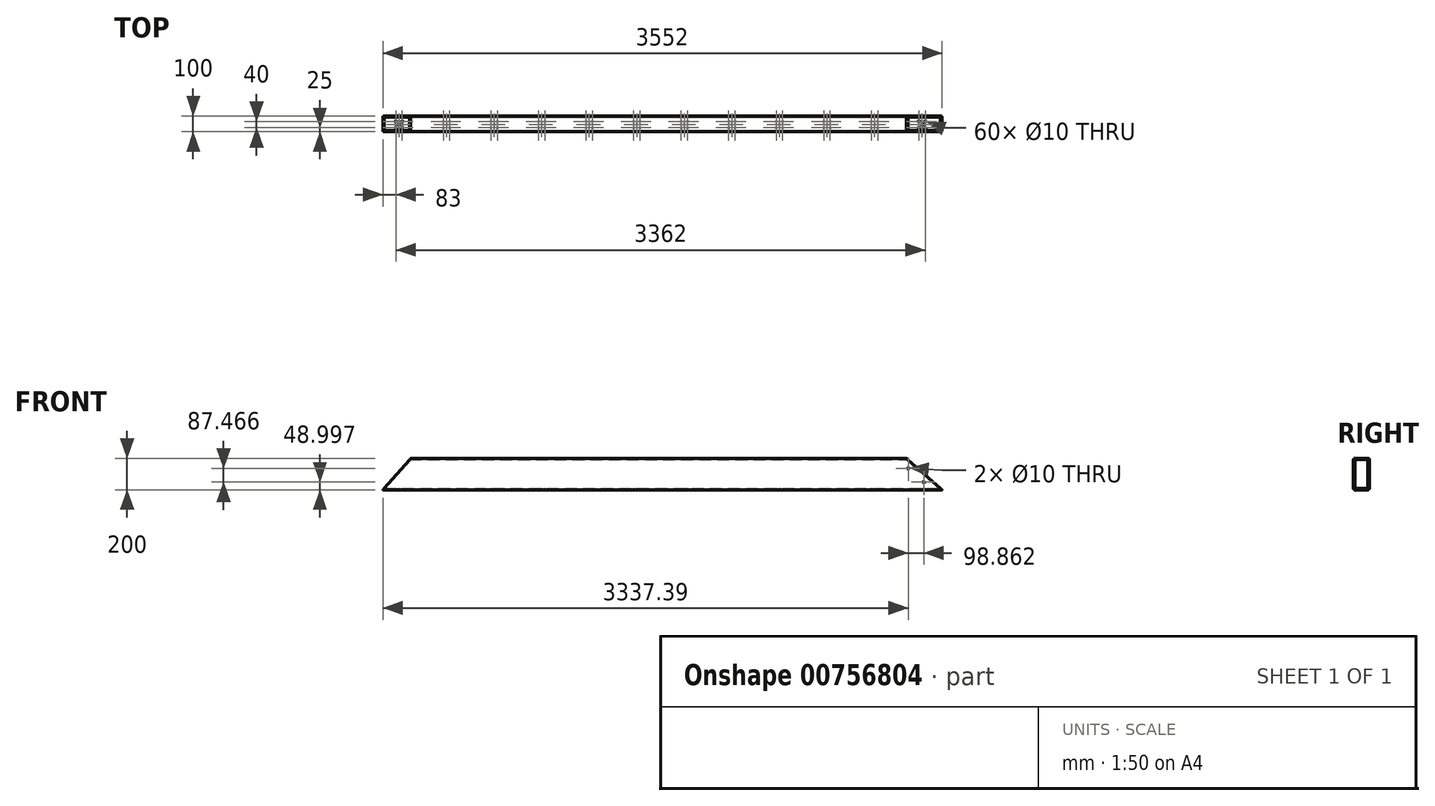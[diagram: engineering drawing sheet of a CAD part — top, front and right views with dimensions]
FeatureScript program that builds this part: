
annotation { "Feature Type Name" : "Feature", "Feature Type Description" : "" }
export const myFeature = defineFeature(function(context is Context, id is Id, definition is map)
    precondition{}
    {
        {
            var Q0;
            Q0=qCreatedBy(makeId("Front.planeOp"),FACE);
            var sketch = newSketch(context, id + "F0", { "sketchPlane" : qUnion([Q0])});
            skLineSegment(sketch, "E0.bottom", {"start": v(280.88, 430.04) * mm, "end": v(-3263.12, 430.04) * mm});
            skLineSegment(sketch, "E0.top", {"start": v(280.88, 230.04) * mm, "end": v(-3263.12, 230.04) * mm});
            skLineSegment(sketch, "E0.left", {"start": v(280.88, 430.04) * mm, "end": v(280.88, 230.04) * mm});
            skLineSegment(sketch, "E0.right", {"start": v(-3263.12, 430.04) * mm, "end": v(-3263.12, 230.04) * mm});
            skSolve(sketch);
        }
        {
            var Q0;
            Q0 = qSketchRegion(id + "F0", true);
            extrude(context, id + "F1", {"entities" : qUnion([Q0]), "depth" : 100 * mm, "offsetDistance" : 25 * mm});
        }
        {
            var Q0;
            Q0=makeQuery(id+"F1.opExtrude","SWEPT_FACE",FACE,{"disambiguationData":[OSD([sQuery(id+"F0.wireOp",EDGE,"E0.left")])]});
            var sketch = newSketch(context, id + "F2", { "sketchPlane" : qUnion([Q0])});
            skLineSegment(sketch, "E1.bottom", {"start": v(-92, 422.04) * mm, "end": v(-8, 422.04) * mm});
            skLineSegment(sketch, "E1.top", {"start": v(-92, 238.04) * mm, "end": v(-8, 238.04) * mm});
            skLineSegment(sketch, "E1.left", {"start": v(-92, 422.04) * mm, "end": v(-92, 238.04) * mm});
            skLineSegment(sketch, "E1.right", {"start": v(-8, 422.04) * mm, "end": v(-8, 238.04) * mm});
            skSolve(sketch);
        }
        {
            var Q0;
            Q0=makeQuery(id+"F2.imprint","IMPRINT",FACE,{"disambiguationData":[TD([[makeQuery(id+"F2.imprint","IMPRINT",EDGE,{"derivedFrom":sQuery(id+"F2.wireOp",EDGE,"E1.bottom")}),-1.0]])]});
            extrude(context, id + "F3", {"entities" : qUnion([Q0]), "operationType" : NewBodyOperationType.REMOVE, "oppositeDirection" : true, "depth" : 3550 * mm, "offsetDistance" : 25 * mm});
        }
        {
            var Q0;
            Q0=makeQuery(id+"F1.opExtrude","SWEPT_FACE",FACE,{"disambiguationData":[OSD([sQuery(id+"F0.wireOp",EDGE,"E0.bottom")])]});
            var sketch = newSketch(context, id + "F4", { "sketchPlane" : qUnion([Q0])});
            skCircle(sketch, "E2", {"center": v(-1234.85, -45) * mm, "radius": 5 * mm});
            skCircle(sketch, "E3", {"center": v(-1254.85, -75) * mm, "radius": 5 * mm});
            skCircle(sketch, "E4", {"center": v(-1214.85, -75) * mm, "radius": 5 * mm});
            skCircle(sketch, "E5", {"center": v(-1254.85, -25) * mm, "radius": 5 * mm});
            skCircle(sketch, "E6", {"center": v(-1214.85, -25) * mm, "radius": 5 * mm});
            skSolve(sketch);
        }
        {
            var Q0;
            Q0=makeQuery(id+"F1.opExtrude","SWEPT_FACE",FACE,{"disambiguationData":[OSD([sQuery(id+"F0.wireOp",EDGE,"E0.left")])]});
            var Q1;
            Q1=sQuery(id+"F4.wireOp",EDGE,"E3");
            var Q2;
            Q2=sQuery(id+"F4.wireOp",EDGE,"E5");
            var Q3;
            Q3=sQuery(id+"F4.wireOp",EDGE,"E6");
            var Q4;
            Q4=sQuery(id+"F4.wireOp",EDGE,"E4");
            var Q5;
            Q5=sQuery(id+"F4.wireOp",EDGE,"E2");
            extrude(context, id + "F5", {"entities" : qUnion([Q0]), "operationType" : NewBodyOperationType.ADD, "surfaceEntities" : qUnion([Q1, Q2, Q3, Q4, Q5]), "depth" : 8 * mm, "offsetDistance" : 25 * mm});
        }
        {
            var Q0;
            Q0=makeQuery(id+"F1.opExtrude","SWEPT_FACE",FACE,{"disambiguationData":[OSD([sQuery(id+"F0.wireOp",EDGE,"E0.top")])]});
            var sketch = newSketch(context, id + "F6", { "sketchPlane" : qUnion([Q0])});
            skCircle(sketch, "E7", {"center": v(-3180.12, 75) * mm, "radius": 5 * mm});
            skCircle(sketch, "E8", {"center": v(-3140.12, 75) * mm, "radius": 5 * mm});
            skCircle(sketch, "E9", {"center": v(-3160.12, 55) * mm, "radius": 5 * mm});
            skCircle(sketch, "E10", {"center": v(-3180.12, 35) * mm, "radius": 5 * mm});
            skCircle(sketch, "E11", {"center": v(-3140.12, 35) * mm, "radius": 5 * mm});
            skCircle(sketch, "E12", {"center": v(-2878.12, 75) * mm, "radius": 5 * mm});
            skCircle(sketch, "E13", {"center": v(-2838.12, 75) * mm, "radius": 5 * mm});
            skCircle(sketch, "E14", {"center": v(-2858.12, 55) * mm, "radius": 5 * mm});
            skCircle(sketch, "E15", {"center": v(-2878.12, 35) * mm, "radius": 5 * mm});
            skCircle(sketch, "E16", {"center": v(-2838.12, 35) * mm, "radius": 5 * mm});
            skCircle(sketch, "E17", {"center": v(-2576.12, 75) * mm, "radius": 5 * mm});
            skCircle(sketch, "E18", {"center": v(-2536.12, 75) * mm, "radius": 5 * mm});
            skCircle(sketch, "E19", {"center": v(-2556.12, 55) * mm, "radius": 5 * mm});
            skCircle(sketch, "E20", {"center": v(-2576.12, 35) * mm, "radius": 5 * mm});
            skCircle(sketch, "E21", {"center": v(-2536.12, 35) * mm, "radius": 5 * mm});
            skCircle(sketch, "E22", {"center": v(-2274.12, 75) * mm, "radius": 5 * mm});
            skCircle(sketch, "E23", {"center": v(-2234.12, 75) * mm, "radius": 5 * mm});
            skCircle(sketch, "E24", {"center": v(-2254.12, 55) * mm, "radius": 5 * mm});
            skCircle(sketch, "E25", {"center": v(-2274.12, 35) * mm, "radius": 5 * mm});
            skCircle(sketch, "E26", {"center": v(-2234.12, 35) * mm, "radius": 5 * mm});
            skCircle(sketch, "E27", {"center": v(-1972.12, 75) * mm, "radius": 5 * mm});
            skCircle(sketch, "E28", {"center": v(-1932.12, 75) * mm, "radius": 5 * mm});
            skCircle(sketch, "E29", {"center": v(-1952.12, 55) * mm, "radius": 5 * mm});
            skCircle(sketch, "E30", {"center": v(-1972.12, 35) * mm, "radius": 5 * mm});
            skCircle(sketch, "E31", {"center": v(-1932.12, 35) * mm, "radius": 5 * mm});
            skCircle(sketch, "E32", {"center": v(-1670.12, 75) * mm, "radius": 5 * mm});
            skCircle(sketch, "E33", {"center": v(-1630.12, 75) * mm, "radius": 5 * mm});
            skCircle(sketch, "E34", {"center": v(-1650.12, 55) * mm, "radius": 5 * mm});
            skCircle(sketch, "E35", {"center": v(-1670.12, 35) * mm, "radius": 5 * mm});
            skCircle(sketch, "E36", {"center": v(-1630.12, 35) * mm, "radius": 5 * mm});
            skCircle(sketch, "E37", {"center": v(-1368.12, 75) * mm, "radius": 5 * mm});
            skCircle(sketch, "E38", {"center": v(-1328.12, 75) * mm, "radius": 5 * mm});
            skCircle(sketch, "E39", {"center": v(-1348.12, 55) * mm, "radius": 5 * mm});
            skCircle(sketch, "E40", {"center": v(-1368.12, 35) * mm, "radius": 5 * mm});
            skCircle(sketch, "E41", {"center": v(-1328.12, 35) * mm, "radius": 5 * mm});
            skCircle(sketch, "E42", {"center": v(-1066.12, 75) * mm, "radius": 5 * mm});
            skCircle(sketch, "E43", {"center": v(-1026.12, 75) * mm, "radius": 5 * mm});
            skCircle(sketch, "E44", {"center": v(-1046.12, 55) * mm, "radius": 5 * mm});
            skCircle(sketch, "E45", {"center": v(-1066.12, 35) * mm, "radius": 5 * mm});
            skCircle(sketch, "E46", {"center": v(-1026.12, 35) * mm, "radius": 5 * mm});
            skCircle(sketch, "E47", {"center": v(-764.12, 75) * mm, "radius": 5 * mm});
            skCircle(sketch, "E48", {"center": v(-724.12, 75) * mm, "radius": 5 * mm});
            skCircle(sketch, "E49", {"center": v(-744.12, 55) * mm, "radius": 5 * mm});
            skCircle(sketch, "E50", {"center": v(-764.12, 35) * mm, "radius": 5 * mm});
            skCircle(sketch, "E51", {"center": v(-724.12, 35) * mm, "radius": 5 * mm});
            skCircle(sketch, "E52", {"center": v(-160.12, 75) * mm, "radius": 5 * mm});
            skCircle(sketch, "E53", {"center": v(-120.12, 75) * mm, "radius": 5 * mm});
            skCircle(sketch, "E54", {"center": v(-140.12, 55) * mm, "radius": 5 * mm});
            skCircle(sketch, "E55", {"center": v(-160.12, 35) * mm, "radius": 5 * mm});
            skCircle(sketch, "E56", {"center": v(-120.12, 35) * mm, "radius": 5 * mm});
            skCircle(sketch, "E57", {"center": v(141.88, 75) * mm, "radius": 5 * mm});
            skCircle(sketch, "E58", {"center": v(181.88, 75) * mm, "radius": 5 * mm});
            skCircle(sketch, "E59", {"center": v(161.88, 55) * mm, "radius": 5 * mm});
            skCircle(sketch, "E60", {"center": v(141.88, 35) * mm, "radius": 5 * mm});
            skCircle(sketch, "E61", {"center": v(181.88, 35) * mm, "radius": 5 * mm});
            skCircle(sketch, "E62", {"center": v(-462.12, 75) * mm, "radius": 5 * mm});
            skCircle(sketch, "E63", {"center": v(-422.12, 75) * mm, "radius": 5 * mm});
            skCircle(sketch, "E64", {"center": v(-442.12, 55) * mm, "radius": 5 * mm});
            skCircle(sketch, "E65", {"center": v(-462.12, 35) * mm, "radius": 5 * mm});
            skCircle(sketch, "E66", {"center": v(-422.12, 35) * mm, "radius": 5 * mm});
            skSolve(sketch);
        }
        {
            var Q0;
            Q0 = qSketchRegion(id + "F6", true);
            extrude(context, id + "F7", {"entities" : qUnion([Q0]), "operationType" : NewBodyOperationType.REMOVE, "oppositeDirection" : true, "depth" : 8 * mm, "offsetDistance" : 25 * mm});
        }
        {
            var Q0;
            {var subQ0=sQuery(id+"F0.wireOp",EDGE,"E0.left");Q0=makeQuery(id+"F5.boolean.opBoolean","MERGE",FACE,{"derivedFrom":[makeQuery(id+"F1.opExtrude","CAP_FACE",FACE,{"disambiguationData":[OSD([sQuery(id+"F0.wireOp",EDGE,"E0.bottom"),sQuery(id+"F0.wireOp",EDGE,"E0.top"),subQ0,sQuery(id+"F0.wireOp",EDGE,"E0.right")])],"isStart":true}),makeQuery(id+"F5.opExtrude","SWEPT_FACE",FACE,{"disambiguationData":[OSD([subQ0]),TDD([makeQuery(id+"F1.opExtrude","CAP_EDGE",EDGE,{"disambiguationData":[OSD([subQ0])],"isStart":true})])]})]});}
            var sketch = newSketch(context, id + "F8", { "sketchPlane" : qUnion([Q0])});
            skLineSegment(sketch, "E67", {"start": v(3086.18, 430.04) * mm, "end": v(3263.12, 230.04) * mm});
            skLineSegment(sketch, "E68", {"start": v(-62.82, 430.04) * mm, "end": v(-288.88, 230.04) * mm});
            skSolve(sketch);
        }
        {
            var Q0;
            {var subQ0=sQuery(id+"F8.wireOp",EDGE,"E68");Q0=makeQuery(id+"F8.imprint","IMPRINT",FACE,{"disambiguationData":[TD([[makeQuery(id+"F8.imprint","IMPRINT",EDGE,{"derivedFrom":subQ0}),-1.0]])]});}
            var Q1;
            Q1=sQuery(id+"F8.wireOp",EDGE,"E68");
            extrude(context, id + "F9", {"entities" : qUnion([Q0]), "operationType" : NewBodyOperationType.REMOVE, "surfaceEntities" : qUnion([Q1]), "oppositeDirection" : true, "depth" : 100 * mm, "offsetDistance" : 25 * mm});
        }
        {
            var Q0;
            {var subQ0=sQuery(id+"F8.wireOp",EDGE,"E67");Q0=makeQuery(id+"F8.imprint","IMPRINT",FACE,{"disambiguationData":[TD([[makeQuery(id+"F8.imprint","IMPRINT",EDGE,{"derivedFrom":subQ0}),1.0]])]});}
            var Q1;
            Q1=sQuery(id+"F8.wireOp",EDGE,"E67");
            extrude(context, id + "F10", {"entities" : qUnion([Q0]), "operationType" : NewBodyOperationType.REMOVE, "surfaceEntities" : qUnion([Q1]), "oppositeDirection" : true, "depth" : 100 * mm, "offsetDistance" : 25 * mm});
        }
        {
            var Q0;
            {var subQ0=sQuery(id+"F0.wireOp",EDGE,"E0.left");var subQ1=sQuery(id+"F0.wireOp",EDGE,"E0.top");Q0=makeQuery(id+"F5.boolean.opBoolean","MERGE",EDGE,{"derivedFrom":[makeQuery(id+"F1.opExtrude","CAP_EDGE",EDGE,{"disambiguationData":[OSD([subQ1])],"isStart":true}),makeQuery(id+"F5.opExtrude","SWEPT_EDGE",EDGE,{"disambiguationData":[OSD([subQ1,subQ0]),TDD([makeQuery(id+"F1.opExtrude","CAP_VERTEX",VERTEX,{"disambiguationData":[OSD([subQ1,subQ0])],"isStart":true})])]})]});}
            var Q1;
            {var subQ0=sQuery(id+"F0.wireOp",EDGE,"E0.left");var subQ1=sQuery(id+"F0.wireOp",EDGE,"E0.top");Q1=makeQuery(id+"F5.boolean.opBoolean","MERGE",EDGE,{"derivedFrom":[makeQuery(id+"F1.opExtrude","CAP_EDGE",EDGE,{"disambiguationData":[OSD([subQ1])],"isStart":false}),makeQuery(id+"F5.opExtrude","SWEPT_EDGE",EDGE,{"disambiguationData":[OSD([subQ1,subQ0]),TDD([makeQuery(id+"F1.opExtrude","CAP_VERTEX",VERTEX,{"disambiguationData":[OSD([subQ1,subQ0])],"isStart":false})])]})]});}
            var Q2;
            {var subQ0=sQuery(id+"F0.wireOp",EDGE,"E0.left");var subQ1=sQuery(id+"F0.wireOp",EDGE,"E0.bottom");Q2=makeQuery(id+"F5.boolean.opBoolean","MERGE",EDGE,{"derivedFrom":[makeQuery(id+"F1.opExtrude","CAP_EDGE",EDGE,{"disambiguationData":[OSD([subQ1])],"isStart":false}),makeQuery(id+"F5.opExtrude","SWEPT_EDGE",EDGE,{"disambiguationData":[OSD([subQ1,subQ0]),TDD([makeQuery(id+"F1.opExtrude","CAP_VERTEX",VERTEX,{"disambiguationData":[OSD([subQ1,subQ0])],"isStart":false})])]})]});}
            var Q3;
            {var subQ0=sQuery(id+"F0.wireOp",EDGE,"E0.left");var subQ1=sQuery(id+"F0.wireOp",EDGE,"E0.bottom");Q3=makeQuery(id+"F5.boolean.opBoolean","MERGE",EDGE,{"derivedFrom":[makeQuery(id+"F1.opExtrude","CAP_EDGE",EDGE,{"disambiguationData":[OSD([subQ1])],"isStart":true}),makeQuery(id+"F5.opExtrude","SWEPT_EDGE",EDGE,{"disambiguationData":[OSD([subQ1,subQ0]),TDD([makeQuery(id+"F1.opExtrude","CAP_VERTEX",VERTEX,{"disambiguationData":[OSD([subQ1,subQ0])],"isStart":true})])]})]});}
            fillet(context, id + "F11", {"entities" : qUnion([Q0, Q1, Q2, Q3]), "radius" : 9 * mm, "tangentPropagation" : true, "defaultsChanged" : false, "vertexSettings" : [], "allowEdgeOverflow" : false});
        }
        {
            var Q0;
            {var subQ0=sQuery(id+"F2.wireOp",EDGE,"E1.left");var subQ1=sQuery(id+"F2.wireOp",EDGE,"E1.top");Q0=makeQuery(id+"F5.boolean.opBoolean","MERGE",EDGE,{"derivedFrom":[makeQuery(id+"F3.boolean.opBoolean","COPY",EDGE,{"derivedFrom":makeQuery(id+"F3.opExtrude","SWEPT_EDGE",EDGE,{"disambiguationData":[OSD([subQ1,subQ0])]})}),makeQuery(id+"F5.opExtrude","SWEPT_EDGE",EDGE,{"disambiguationData":[OSD([subQ1,subQ0])]})]});}
            var Q1;
            {var subQ0=sQuery(id+"F2.wireOp",EDGE,"E1.right");var subQ1=sQuery(id+"F2.wireOp",EDGE,"E1.top");Q1=makeQuery(id+"F5.boolean.opBoolean","MERGE",EDGE,{"derivedFrom":[makeQuery(id+"F3.boolean.opBoolean","COPY",EDGE,{"derivedFrom":makeQuery(id+"F3.opExtrude","SWEPT_EDGE",EDGE,{"disambiguationData":[OSD([subQ1,subQ0])]})}),makeQuery(id+"F5.opExtrude","SWEPT_EDGE",EDGE,{"disambiguationData":[OSD([subQ1,subQ0])]})]});}
            var Q2;
            {var subQ0=sQuery(id+"F2.wireOp",EDGE,"E1.right");var subQ1=sQuery(id+"F2.wireOp",EDGE,"E1.bottom");Q2=makeQuery(id+"F5.boolean.opBoolean","MERGE",EDGE,{"derivedFrom":[makeQuery(id+"F3.boolean.opBoolean","COPY",EDGE,{"derivedFrom":makeQuery(id+"F3.opExtrude","SWEPT_EDGE",EDGE,{"disambiguationData":[OSD([subQ1,subQ0])]})}),makeQuery(id+"F5.opExtrude","SWEPT_EDGE",EDGE,{"disambiguationData":[OSD([subQ1,subQ0])]})]});}
            var Q3;
            {var subQ0=sQuery(id+"F2.wireOp",EDGE,"E1.left");var subQ1=sQuery(id+"F2.wireOp",EDGE,"E1.bottom");Q3=makeQuery(id+"F5.boolean.opBoolean","MERGE",EDGE,{"derivedFrom":[makeQuery(id+"F3.boolean.opBoolean","COPY",EDGE,{"derivedFrom":makeQuery(id+"F3.opExtrude","SWEPT_EDGE",EDGE,{"disambiguationData":[OSD([subQ1,subQ0])]})}),makeQuery(id+"F5.opExtrude","SWEPT_EDGE",EDGE,{"disambiguationData":[OSD([subQ1,subQ0])]})]});}
            fillet(context, id + "F12", {"entities" : qUnion([Q0, Q1, Q2, Q3]), "radius" : 6 * mm, "tangentPropagation" : true, "allowEdgeOverflow" : false});
        }
        {
            var Q0;
            {var subQ0=sQuery(id+"F0.wireOp",EDGE,"E0.left");Q0=makeQuery(id+"F5.boolean.opBoolean","MERGE",FACE,{"derivedFrom":[makeQuery(id+"F1.opExtrude","CAP_FACE",FACE,{"disambiguationData":[OSD([sQuery(id+"F0.wireOp",EDGE,"E0.bottom"),sQuery(id+"F0.wireOp",EDGE,"E0.top"),subQ0,sQuery(id+"F0.wireOp",EDGE,"E0.right")])],"isStart":false}),makeQuery(id+"F5.opExtrude","SWEPT_FACE",FACE,{"disambiguationData":[OSD([subQ0]),TDD([makeQuery(id+"F1.opExtrude","CAP_EDGE",EDGE,{"disambiguationData":[OSD([subQ0])],"isStart":false})])]})]});}
            var sketch = newSketch(context, id + "F13", { "sketchPlane" : qUnion([Q0])});
            skCircle(sketch, "E69", {"center": v(173.13, 279.04) * mm, "radius": 5 * mm});
            skCircle(sketch, "E70", {"center": v(74.27, 366.5) * mm, "radius": 5 * mm});
            skSolve(sketch);
        }
        {
            var Q0;
            Q0 = qSketchRegion(id + "F13", true);
            extrude(context, id + "F14", {"entities" : qUnion([Q0]), "operationType" : NewBodyOperationType.REMOVE, "oppositeDirection" : true, "depth" : 25 * mm, "offsetDistance" : 25 * mm});
        }
    });
